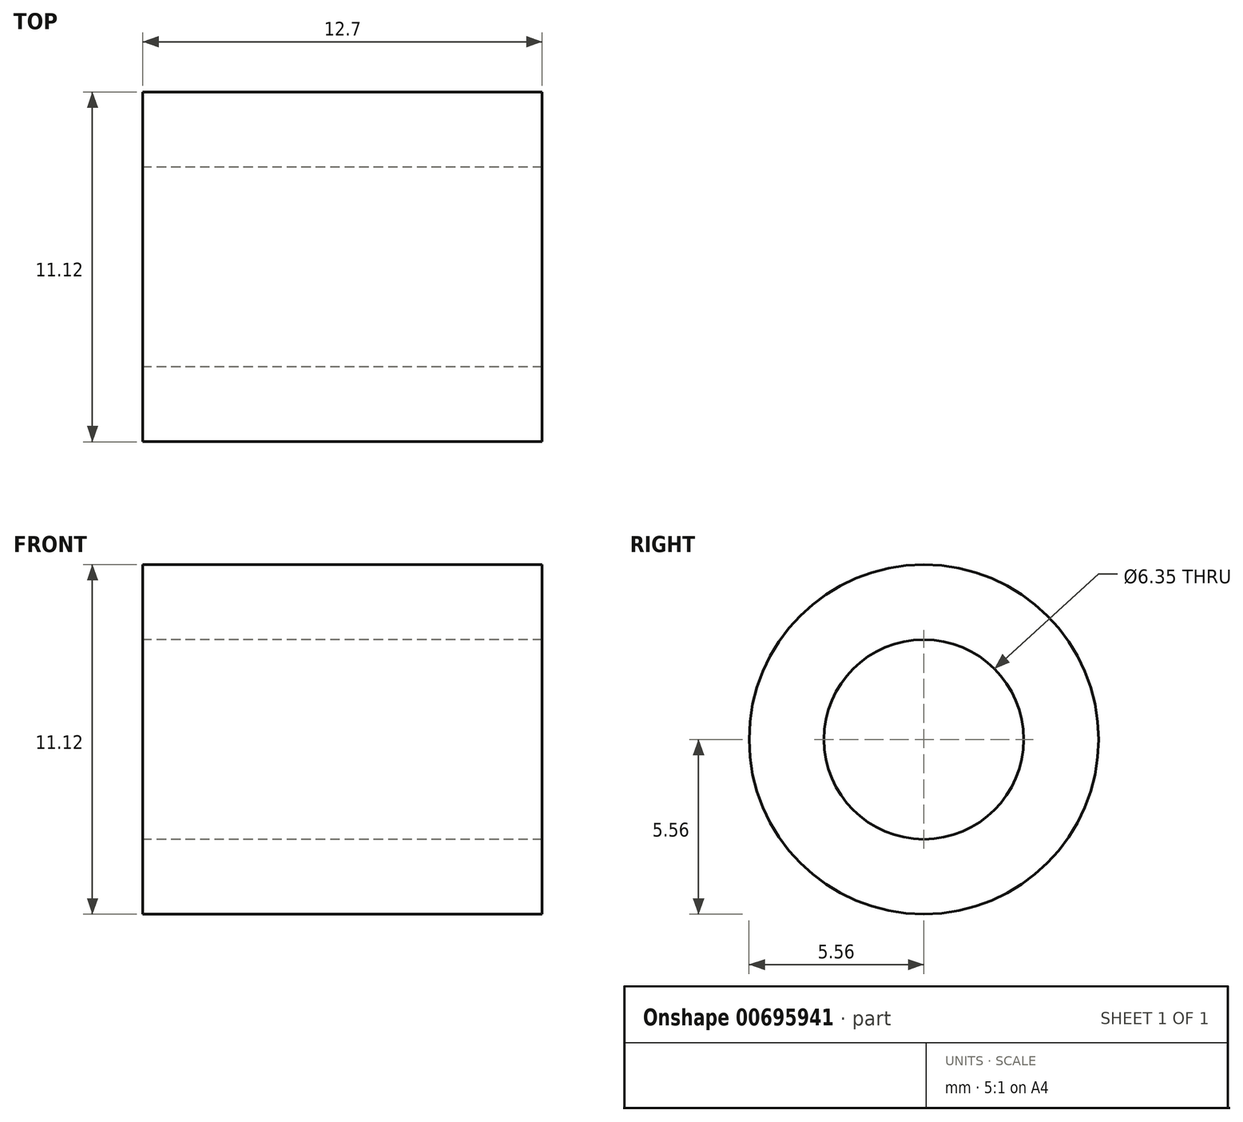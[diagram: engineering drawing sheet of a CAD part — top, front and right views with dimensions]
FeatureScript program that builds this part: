
annotation { "Feature Type Name" : "Feature", "Feature Type Description" : "" }
export const myFeature = defineFeature(function(context is Context, id is Id, definition is map)
    precondition{}
    {
        {
            var Q0;
            Q0=qCreatedBy(makeId("Right.planeOp"),FACE);
            var sketch = newSketch(context, id + "F0", { "sketchPlane" : qUnion([Q0])});
            skCircle(sketch, "E0", {"center": v(0, 0) * mm, "radius": 5.56 * mm});
            skCircle(sketch, "E1", {"center": v(0, 0) * mm, "radius": 3.18 * mm});
            skSolve(sketch);
        }
        {
            var Q0;
            Q0 = qSketchRegion(id + "F0", true);
            extrude(context, id + "F1", {"entities" : qUnion([Q0]), "endBound" : BoundingType.SYMMETRIC, "depth" : 12.7 * mm, "offsetDistance" : 25 * mm});
        }
    });
